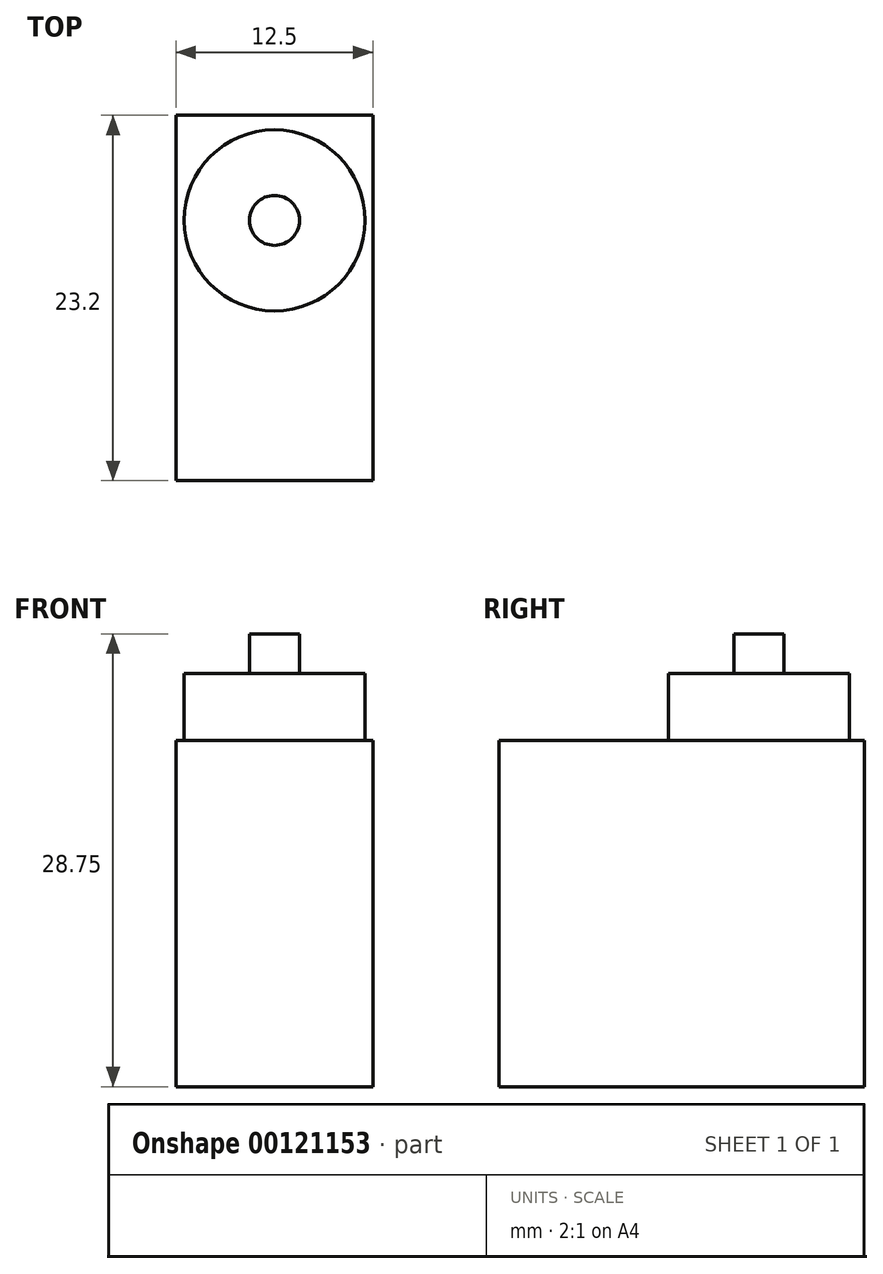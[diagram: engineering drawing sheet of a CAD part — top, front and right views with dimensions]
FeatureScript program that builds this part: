
annotation { "Feature Type Name" : "Feature", "Feature Type Description" : "" }
export const myFeature = defineFeature(function(context is Context, id is Id, definition is map)
    precondition{}
    {
        {
            var Q0;
            Q0=qCreatedBy(makeId("Top.planeOp"),FACE);
            var sketch = newSketch(context, id + "F0", { "sketchPlane" : qUnion([Q0])});
            skLineSegment(sketch, "E0.bottom", {"start": v(-60.5, 2.84) * mm, "end": v(-48, 2.84) * mm});
            skLineSegment(sketch, "E0.top", {"start": v(-60.5, -20.36) * mm, "end": v(-48, -20.36) * mm});
            skLineSegment(sketch, "E0.left", {"start": v(-60.5, 2.84) * mm, "end": v(-60.5, -20.36) * mm});
            skLineSegment(sketch, "E0.right", {"start": v(-48, 2.84) * mm, "end": v(-48, -20.36) * mm});
            skCircle(sketch, "E1", {"center": v(-54.25, -3.83) * mm, "radius": 5.75 * mm});
            skCircle(sketch, "E2", {"center": v(-54.25, -3.83) * mm, "radius": 1.59 * mm});
            skSolve(sketch);
        }
        {
            var Q0;
            Q0=makeQuery(id+"F0.imprint","IMPRINT",FACE,{"disambiguationData":[TD([[makeQuery(id+"F0.imprint","IMPRINT",EDGE,{"derivedFrom":sQuery(id+"F0.wireOp",EDGE,"E0.top")}),1.0]])]});
            var Q1;
            Q1=makeQuery(id+"F0.imprint","IMPRINT",FACE,{"disambiguationData":[TD([[makeQuery(id+"F0.imprint","IMPRINT",EDGE,{"derivedFrom":sQuery(id+"F0.wireOp",EDGE,"E1")}),1.0]])]});
            var Q2;
            Q2=makeQuery(id+"F0.imprint","IMPRINT",FACE,{"disambiguationData":[TD([[makeQuery(id+"F0.imprint","IMPRINT",EDGE,{"derivedFrom":sQuery(id+"F0.wireOp",EDGE,"E2")}),1.0]])]});
            extrude(context, id + "F1", {"entities" : qUnion([Q0, Q1, Q2]), "depth" : 22 * mm});
        }
        {
            var Q0;
            Q0=makeQuery(id+"F0.imprint","IMPRINT",FACE,{"disambiguationData":[TD([[makeQuery(id+"F0.imprint","IMPRINT",EDGE,{"derivedFrom":sQuery(id+"F0.wireOp",EDGE,"E1")}),1.0]])]});
            var Q1;
            Q1=makeQuery(id+"F0.imprint","IMPRINT",FACE,{"disambiguationData":[TD([[makeQuery(id+"F0.imprint","IMPRINT",EDGE,{"derivedFrom":sQuery(id+"F0.wireOp",EDGE,"E2")}),1.0]])]});
            extrude(context, id + "F2", {"entities" : qUnion([Q0, Q1]), "operationType" : NewBodyOperationType.ADD, "depth" : 26.25 * mm});
        }
        {
            var Q0;
            Q0=makeQuery(id+"F0.imprint","IMPRINT",FACE,{"disambiguationData":[TD([[makeQuery(id+"F0.imprint","IMPRINT",EDGE,{"derivedFrom":sQuery(id+"F0.wireOp",EDGE,"E2")}),1.0]])]});
            extrude(context, id + "F3", {"entities" : qUnion([Q0]), "operationType" : NewBodyOperationType.ADD, "depth" : 28.75 * mm});
        }
    });
